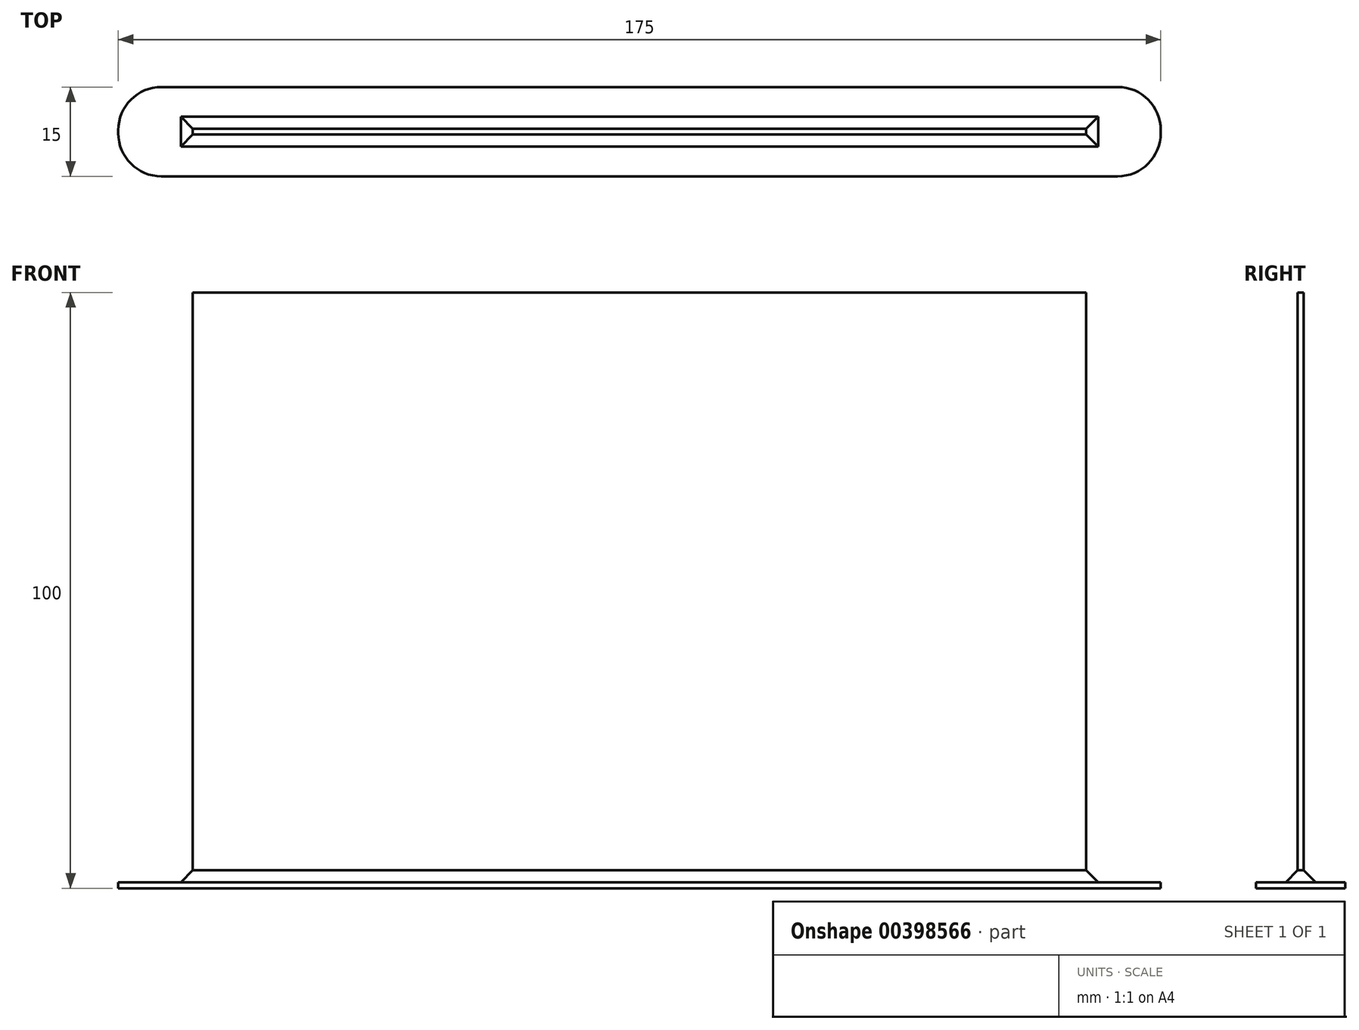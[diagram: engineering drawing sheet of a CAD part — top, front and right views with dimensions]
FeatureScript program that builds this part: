
annotation { "Feature Type Name" : "Feature", "Feature Type Description" : "" }
export const myFeature = defineFeature(function(context is Context, id is Id, definition is map)
    precondition{}
    {
        {
            var Q0;
            Q0=qCreatedBy(makeId("Top.planeOp"),FACE);
            var sketch = newSketch(context, id + "F0", { "sketchPlane" : qUnion([Q0])});
            skLineSegment(sketch, "E0.bottom", {"start": v(75, -0.5) * mm, "end": v(-75, -0.5) * mm});
            skLineSegment(sketch, "E0.top", {"start": v(75, 0.5) * mm, "end": v(-75, 0.5) * mm});
            skLineSegment(sketch, "E0.left", {"start": v(75, -0.5) * mm, "end": v(75, 0.5) * mm});
            skLineSegment(sketch, "E0.right", {"start": v(-75, -0.5) * mm, "end": v(-75, 0.5) * mm});
            skPoint(sketch, "E0.middle", {"position": v(0, 0) * mm});
            skSolve(sketch);
        }
        {
            var Q0;
            Q0 = qSketchRegion(id + "F0", true);
            extrude(context, id + "F1", {"entities" : qUnion([Q0]), "depth" : 100 * mm});
        }
        {
            var Q0;
            Q0=qCreatedBy(makeId("Top.planeOp"),FACE);
            var sketch = newSketch(context, id + "F2", { "sketchPlane" : qUnion([Q0])});
            skLineSegment(sketch, "E1.bottom", {"start": v(87.5, -7.5) * mm, "end": v(-87.5, -7.5) * mm});
            skLineSegment(sketch, "E1.top", {"start": v(87.5, 7.5) * mm, "end": v(-87.5, 7.5) * mm});
            skLineSegment(sketch, "E1.left", {"start": v(87.5, -7.5) * mm, "end": v(87.5, 7.5) * mm});
            skLineSegment(sketch, "E1.right", {"start": v(-87.5, -7.5) * mm, "end": v(-87.5, 7.5) * mm});
            skPoint(sketch, "E1.middle", {"position": v(0, 0) * mm});
            skSolve(sketch);
        }
        {
            var Q0;
            Q0 = qSketchRegion(id + "F2", true);
            extrude(context, id + "F3", {"entities" : qUnion([Q0]), "operationType" : NewBodyOperationType.ADD, "depth" : 1 * mm});
        }
        {
            var Q0;
            Q0=makeQuery(id+"F3.opExtrude","SWEPT_EDGE",EDGE,{"disambiguationData":[OSD([sQuery(id+"F2.wireOp",EDGE,"E1.bottom"),sQuery(id+"F2.wireOp",EDGE,"E1.right")])]});
            var Q1;
            Q1=makeQuery(id+"F3.opExtrude","SWEPT_EDGE",EDGE,{"disambiguationData":[OSD([sQuery(id+"F2.wireOp",EDGE,"E1.top"),sQuery(id+"F2.wireOp",EDGE,"E1.right")])]});
            var Q2;
            Q2=makeQuery(id+"F3.opExtrude","SWEPT_EDGE",EDGE,{"disambiguationData":[OSD([sQuery(id+"F2.wireOp",EDGE,"E1.bottom"),sQuery(id+"F2.wireOp",EDGE,"E1.left")])]});
            var Q3;
            Q3=makeQuery(id+"F3.opExtrude","SWEPT_EDGE",EDGE,{"disambiguationData":[OSD([sQuery(id+"F2.wireOp",EDGE,"E1.top"),sQuery(id+"F2.wireOp",EDGE,"E1.left")])]});
            fillet(context, id + "F4", {"entities" : qUnion([Q0, Q1, Q2, Q3]), "radius" : 7.24 * mm, "tangentPropagation" : true, "allowEdgeOverflow" : false});
        }
        {
            var Q0;
            Q0=makeQuery(id+"F3.boolean.opBoolean","INTERSECT",EDGE,{"derivedFrom":[makeQuery(id+"F1.opExtrude","SWEPT_FACE",FACE,{"disambiguationData":[OSD([sQuery(id+"F0.wireOp",EDGE,"E0.top")])]}),makeQuery(id+"F3.opExtrude","CAP_FACE",FACE,{"disambiguationData":[OSD([sQuery(id+"F2.wireOp",EDGE,"E1.bottom"),sQuery(id+"F2.wireOp",EDGE,"E1.top"),sQuery(id+"F2.wireOp",EDGE,"E1.left"),sQuery(id+"F2.wireOp",EDGE,"E1.right")])],"isStart":false})]});
            var Q1;
            Q1=makeQuery(id+"F3.boolean.opBoolean","INTERSECT",EDGE,{"derivedFrom":[makeQuery(id+"F1.opExtrude","SWEPT_FACE",FACE,{"disambiguationData":[OSD([sQuery(id+"F0.wireOp",EDGE,"E0.left")])]}),makeQuery(id+"F3.opExtrude","CAP_FACE",FACE,{"disambiguationData":[OSD([sQuery(id+"F2.wireOp",EDGE,"E1.bottom"),sQuery(id+"F2.wireOp",EDGE,"E1.top"),sQuery(id+"F2.wireOp",EDGE,"E1.left"),sQuery(id+"F2.wireOp",EDGE,"E1.right")])],"isStart":false})]});
            var Q2;
            Q2=makeQuery(id+"F3.boolean.opBoolean","INTERSECT",EDGE,{"derivedFrom":[makeQuery(id+"F1.opExtrude","SWEPT_FACE",FACE,{"disambiguationData":[OSD([sQuery(id+"F0.wireOp",EDGE,"E0.bottom")])]}),makeQuery(id+"F3.opExtrude","CAP_FACE",FACE,{"disambiguationData":[OSD([sQuery(id+"F2.wireOp",EDGE,"E1.bottom"),sQuery(id+"F2.wireOp",EDGE,"E1.top"),sQuery(id+"F2.wireOp",EDGE,"E1.left"),sQuery(id+"F2.wireOp",EDGE,"E1.right")])],"isStart":false})]});
            var Q3;
            Q3=makeQuery(id+"F3.boolean.opBoolean","INTERSECT",EDGE,{"derivedFrom":[makeQuery(id+"F1.opExtrude","SWEPT_FACE",FACE,{"disambiguationData":[OSD([sQuery(id+"F0.wireOp",EDGE,"E0.right")])]}),makeQuery(id+"F3.opExtrude","CAP_FACE",FACE,{"disambiguationData":[OSD([sQuery(id+"F2.wireOp",EDGE,"E1.bottom"),sQuery(id+"F2.wireOp",EDGE,"E1.top"),sQuery(id+"F2.wireOp",EDGE,"E1.left"),sQuery(id+"F2.wireOp",EDGE,"E1.right")])],"isStart":false})]});
            chamfer(context, id + "F5", {"entities" : qUnion([Q0, Q1, Q2, Q3]), "width" : 2 * mm, "tangentPropagation" : true});
        }
    });
